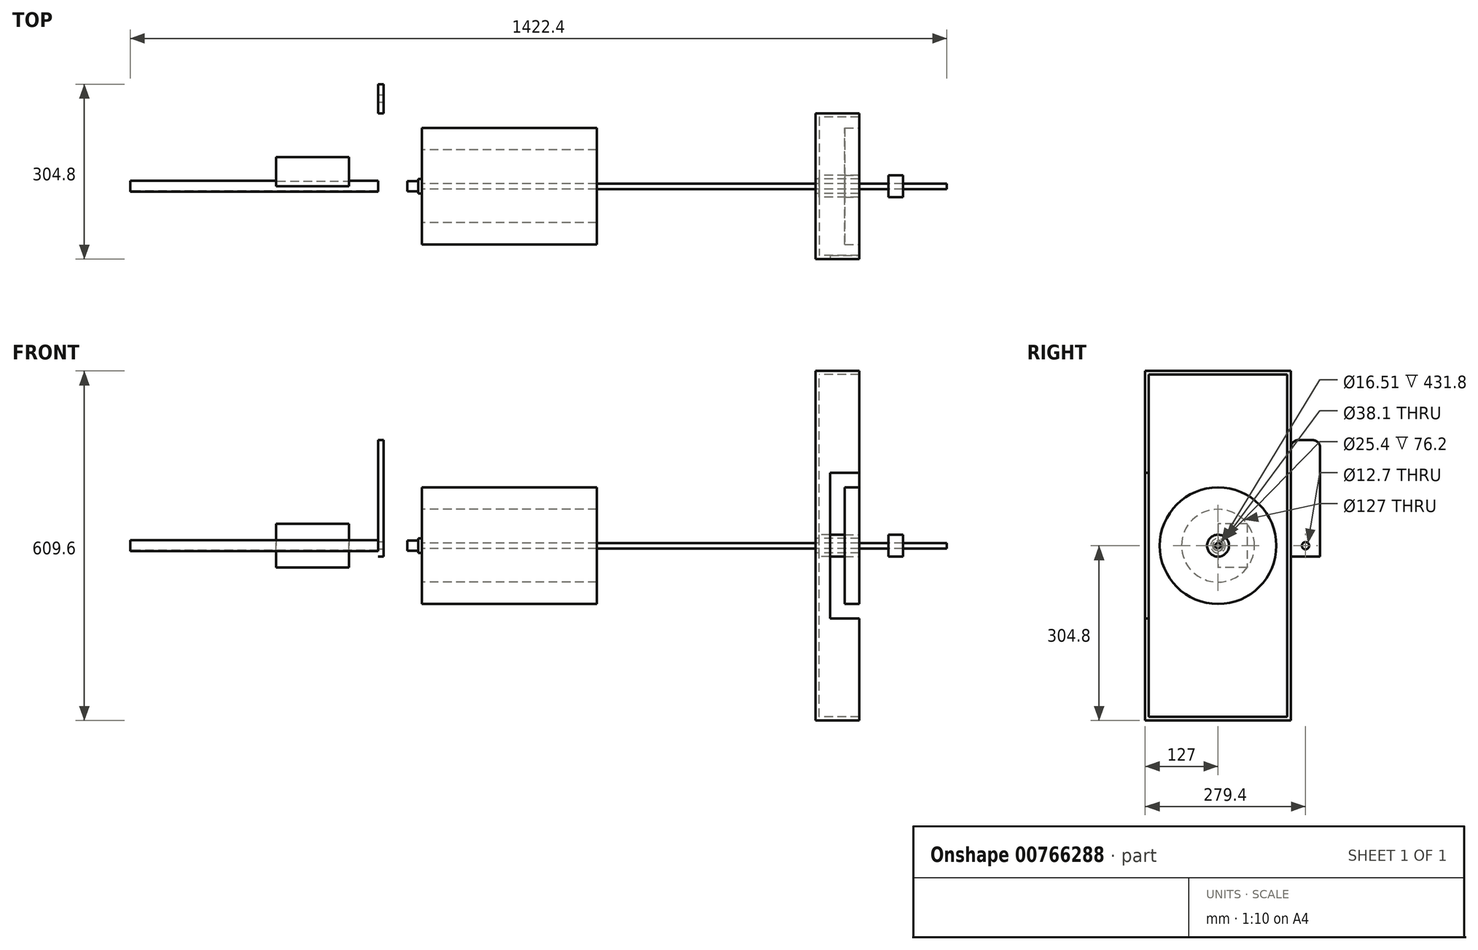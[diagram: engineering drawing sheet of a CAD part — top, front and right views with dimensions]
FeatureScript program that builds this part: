
annotation { "Feature Type Name" : "Feature", "Feature Type Description" : "" }
export const myFeature = defineFeature(function(context is Context, id is Id, definition is map)
    precondition{}
    {
        {
            var Q0;
            Q0=qCreatedBy(makeId("Right.planeOp"),FACE);
            var sketch = newSketch(context, id + "F0", { "sketchPlane" : qUnion([Q0])});
            skCircle(sketch, "E0", {"center": v(0, 0) * mm, "radius": 4.76 * mm});
            skSolve(sketch);
        }
        {
            var Q0;
            Q0=makeQuery(id+"F0.imprint","IMPRINT",FACE,{"disambiguationData":[TD([[makeQuery(id+"F0.imprint","IMPRINT",EDGE,{"derivedFrom":sQuery(id+"F0.wireOp",EDGE,"E0")}),1.0]])]});
            extrude(context, id + "F1", {"entities" : qUnion([Q0]), "depth" : 914.4 * mm, "offsetDistance" : 25.4 * mm});
        }
        {
            var Q0;
            Q0=qCreatedBy(makeId("Right.planeOp"),FACE);
            cPlane(context, id + "F2", {"entities" : qUnion([Q0]), "cplaneType" : CPlaneType.OFFSET, "offset" : 838.2 * mm, "width" : 152.4 * mm, "height" : 152.4 * mm});
        }
        {
            var Q0;
            Q0=qCreatedBy(id+"F2.planeOp",FACE);
            var sketch = newSketch(context, id + "F3", { "sketchPlane" : qUnion([Q0])});
            skCircle(sketch, "E1", {"center": v(0, 0) * mm, "radius": 19.05 * mm});
            skSolve(sketch);
        }
        {
            var Q0;
            Q0=makeQuery(id+"F3.imprint","IMPRINT",FACE,{"disambiguationData":[TD([[makeQuery(id+"F3.imprint","IMPRINT",EDGE,{"derivedFrom":sQuery(id+"F3.wireOp",EDGE,"E1")}),1.0]])]});
            extrude(context, id + "F4", {"entities" : qUnion([Q0]), "oppositeDirection" : true, "depth" : 25.4 * mm, "offsetDistance" : 25.4 * mm});
        }
        {
            var Q0;
            Q0=qCreatedBy(makeId("Right.planeOp"),FACE);
            var sketch = newSketch(context, id + "F5", { "sketchPlane" : qUnion([Q0])});
            skCircle(sketch, "E2", {"center": v(0, 0) * mm, "radius": 101.6 * mm});
            skCircle(sketch, "E3", {"center": v(0, 0) * mm, "radius": 63.5 * mm});
            skSolve(sketch);
        }
        {
            var Q0;
            Q0=makeQuery(id+"F5.imprint","IMPRINT",FACE,{"disambiguationData":[TD([[makeQuery(id+"F5.imprint","IMPRINT",EDGE,{"derivedFrom":sQuery(id+"F5.wireOp",EDGE,"E2")}),1.0]])]});
            extrude(context, id + "F6", {"entities" : qUnion([Q0]), "depth" : 304.8 * mm, "offsetDistance" : 25.4 * mm});
        }
        {
            var Q0;
            Q0=qCreatedBy(id+"F2.planeOp",FACE);
            cPlane(context, id + "F7", {"entities" : qUnion([Q0]), "cplaneType" : CPlaneType.OFFSET, "offset" : 152.4 * mm, "oppositeDirection" : true, "width" : 152.4 * mm, "height" : 152.4 * mm});
        }
        {
            var Q0;
            Q0=qCreatedBy(id+"F7.planeOp",FACE);
            var sketch = newSketch(context, id + "F8", { "sketchPlane" : qUnion([Q0])});
            skCircle(sketch, "E4", {"center": v(0, 0) * mm, "radius": 12.7 * mm});
            skLineSegment(sketch, "E5.bottom", {"start": v(127, -304.8) * mm, "end": v(-127, -304.8) * mm});
            skLineSegment(sketch, "E5.top", {"start": v(127, 304.8) * mm, "end": v(-127, 304.8) * mm});
            skLineSegment(sketch, "E5.left", {"start": v(127, -304.8) * mm, "end": v(127, 304.8) * mm});
            skLineSegment(sketch, "E5.right", {"start": v(-127, -304.8) * mm, "end": v(-127, 304.8) * mm});
            skSolve(sketch);
        }
        {
            var Q0;
            Q0=makeQuery(id+"F8.imprint","IMPRINT",FACE,{"disambiguationData":[TD([[makeQuery(id+"F8.imprint","IMPRINT",EDGE,{"derivedFrom":sQuery(id+"F8.wireOp",EDGE,"E4")}),-1.0]])]});
            extrude(context, id + "F9", {"entities" : qUnion([Q0]), "depth" : 76.2 * mm, "offsetDistance" : 25.4 * mm});
        }
        {
            var Q0;
            Q0=qCreatedBy(makeId("Right.planeOp"),FACE);
            cPlane(context, id + "F10", {"entities" : qUnion([Q0]), "cplaneType" : CPlaneType.OFFSET, "offset" : 254 * mm, "oppositeDirection" : true, "width" : 152.4 * mm, "height" : 152.4 * mm});
        }
        {
            var Q0;
            Q0=qCreatedBy(id+"F10.planeOp",FACE);
            var sketch = newSketch(context, id + "F11", { "sketchPlane" : qUnion([Q0])});
            skCircle(sketch, "E6", {"center": v(0, 0) * mm, "radius": 9.53 * mm});
            skLineSegment(sketch, "E7.bottom", {"start": v(50.8, 38.1) * mm, "end": v(-50.8, 38.1) * mm});
            skLineSegment(sketch, "E7.top", {"start": v(50.8, -38.1) * mm, "end": v(-50.8, -38.1) * mm});
            skLineSegment(sketch, "E7.left", {"start": v(50.8, 38.1) * mm, "end": v(50.8, -38.1) * mm});
            skLineSegment(sketch, "E7.right", {"start": v(-50.8, 38.1) * mm, "end": v(-50.8, -38.1) * mm});
            skLineSegment(sketch, "E8", {"start": v(0, 38.1) * mm, "end": v(0, -38.1) * mm});
            skSolve(sketch);
        }
        {
            var Q0;
            {var subQ0=sQuery(id+"F11.wireOp",EDGE,"E7.left");Q0=makeQuery(id+"F11.imprint","IMPRINT",FACE,{"disambiguationData":[TD([[makeQuery(id+"F11.imprint","IMPRINT",EDGE,{"derivedFrom":subQ0}),-1.0]])]});}
            extrude(context, id + "F12", {"entities" : qUnion([Q0]), "depth" : 127 * mm, "offsetDistance" : 25.4 * mm});
        }
        {
            var Q0;
            Q0=qCreatedBy(makeId("Right.planeOp"),FACE);
            cPlane(context, id + "F13", {"entities" : qUnion([Q0]), "cplaneType" : CPlaneType.OFFSET, "offset" : 76.2 * mm, "oppositeDirection" : true, "width" : 152.4 * mm, "height" : 152.4 * mm});
        }
        {
            var Q0;
            Q0=qCreatedBy(id+"F13.planeOp",FACE);
            var sketch = newSketch(context, id + "F14", { "sketchPlane" : qUnion([Q0])});
            skLineSegment(sketch, "E9.bottom", {"start": v(127, -19.05) * mm, "end": v(177.8, -19.05) * mm});
            skLineSegment(sketch, "E9.top", {"start": v(127, 184.15) * mm, "end": v(177.8, 184.15) * mm});
            skLineSegment(sketch, "E9.left", {"start": v(127, -19.05) * mm, "end": v(127, 184.15) * mm});
            skLineSegment(sketch, "E9.right", {"start": v(177.8, -19.05) * mm, "end": v(177.8, 184.15) * mm});
            skPoint(sketch, "E9.middle", {"position": v(152.4, 82.55) * mm});
            skCircle(sketch, "E10", {"center": v(152.4, 0) * mm, "radius": 6.35 * mm});
            skSolve(sketch);
        }
        {
            var Q0;
            Q0=makeQuery(id+"F14.imprint","IMPRINT",FACE,{"disambiguationData":[TD([[makeQuery(id+"F14.imprint","IMPRINT",EDGE,{"derivedFrom":sQuery(id+"F14.wireOp",EDGE,"E9.bottom")}),1.0]])]});
            extrude(context, id + "F15", {"entities" : qUnion([Q0]), "depth" : 9.52 * mm, "offsetDistance" : 25.4 * mm});
        }
        {
            var Q0;
            Q0=makeQuery(id+"F15.opExtrude","SWEPT_EDGE",EDGE,{"disambiguationData":[OSD([sQuery(id+"F14.wireOp",EDGE,"E9.top"),sQuery(id+"F14.wireOp",EDGE,"E9.right")])]});
            var Q1;
            Q1=makeQuery(id+"F15.opExtrude","SWEPT_EDGE",EDGE,{"disambiguationData":[OSD([sQuery(id+"F14.wireOp",EDGE,"E9.top"),sQuery(id+"F14.wireOp",EDGE,"E9.left")])]});
            fillet(context, id + "F16", {"entities" : qUnion([Q0, Q1]), "radius" : 12.7 * mm, "tangentPropagation" : true, "allowEdgeOverflow" : false});
        }
        {
            var Q0;
            Q0=makeQuery(id+"F9.opExtrude","CAP_FACE",FACE,{"disambiguationData":[OSD([sQuery(id+"F8.wireOp",EDGE,"E4"),sQuery(id+"F8.wireOp",EDGE,"E5.bottom"),sQuery(id+"F8.wireOp",EDGE,"E5.top"),sQuery(id+"F8.wireOp",EDGE,"E5.left"),sQuery(id+"F8.wireOp",EDGE,"E5.right")])],"isStart":false});
            shell(context, id + "F17", {"entities" : qUnion([Q0]), "thickness" : 6.35 * mm});
        }
        {
            var Q0;
            {var subQ0=sQuery(id+"F8.wireOp",EDGE,"E5.right");var subQ1=sQuery(id+"F8.wireOp",EDGE,"E5.left");var subQ2=sQuery(id+"F8.wireOp",EDGE,"E5.top");var subQ3=sQuery(id+"F8.wireOp",EDGE,"E5.bottom");var subQ4=sQuery(id+"F8.wireOp",EDGE,"E4");Q0=makeQuery(id+"F17.opShell","OFFSET_FACE",FACE,{"disambiguationData":[OSD([subQ4,subQ3,subQ2,subQ1,subQ0]),TDD([makeQuery(id+"F9.opExtrude","CAP_FACE",FACE,{"disambiguationData":[OSD([subQ4,subQ3,subQ2,subQ1,subQ0])],"isStart":false})])]});}
            var sketch = newSketch(context, id + "F18", { "sketchPlane" : qUnion([Q0])});
            skCircle(sketch, "E11", {"center": v(0, 0) * mm, "radius": 101.6 * mm});
            skSolve(sketch);
        }
        {
            var Q0;
            Q0=makeQuery(id+"F18.imprint","IMPRINT",FACE,{"disambiguationData":[TD([[makeQuery(id+"F18.imprint","IMPRINT",EDGE,{"derivedFrom":sQuery(id+"F18.wireOp",EDGE,"E11")}),1.0]])]});
            extrude(context, id + "F19", {"entities" : qUnion([Q0]), "oppositeDirection" : true, "depth" : 25.4 * mm, "offsetDistance" : 25.4 * mm});
        }
        {
            var Q0;
            Q0=makeQuery(id+"F6.opExtrude","CAP_FACE",FACE,{"disambiguationData":[OSD([sQuery(id+"F5.wireOp",EDGE,"E2"),sQuery(id+"F5.wireOp",EDGE,"E3")])],"isStart":true});
            var sketch = newSketch(context, id + "F20", { "sketchPlane" : qUnion([Q0])});
            skCircle(sketch, "E12", {"center": v(0, 0) * mm, "radius": 12.7 * mm});
            skSolve(sketch);
        }
        {
            var Q0;
            Q0=makeQuery(id+"F20.imprint","IMPRINT",FACE,{"disambiguationData":[TD([[makeQuery(id+"F20.imprint","IMPRINT",EDGE,{"derivedFrom":sQuery(id+"F20.wireOp",EDGE,"E12")}),1.0]])]});
            extrude(context, id + "F21", {"entities" : qUnion([Q0]), "operationType" : NewBodyOperationType.ADD, "depth" : 25.4 * mm, "offsetDistance" : 25.4 * mm});
        }
        {
            var Q0;
            Q0=makeQuery(id+"F21.opExtrude","CAP_FACE",FACE,{"disambiguationData":[OSD([sQuery(id+"F20.wireOp",EDGE,"E12")])],"isStart":false});
            var sketch = newSketch(context, id + "F22", { "sketchPlane" : qUnion([Q0])});
            skCircle(sketch, "E13", {"center": v(0, 0) * mm, "radius": 8.9 * mm});
            skCircle(sketch, "E14", {"center": v(0, 0) * mm, "radius": 12.7 * mm});
            skSolve(sketch);
        }
        {
            var Q0;
            Q0=makeQuery(id+"F22.imprint","IMPRINT",FACE,{"disambiguationData":[TD([[makeQuery(id+"F22.imprint","IMPRINT",EDGE,{"derivedFrom":sQuery(id+"F22.wireOp",EDGE,"E13")}),-1.0]])]});
            extrude(context, id + "F23", {"entities" : qUnion([Q0]), "operationType" : NewBodyOperationType.REMOVE, "oppositeDirection" : true, "depth" : 19.05 * mm, "offsetDistance" : 25.4 * mm});
        }
        {
            var Q0;
            Q0=qCreatedBy(id+"F10.planeOp",FACE);
            cPlane(context, id + "F24", {"entities" : qUnion([Q0]), "cplaneType" : CPlaneType.OFFSET, "offset" : 254 * mm, "oppositeDirection" : true, "width" : 152.4 * mm, "height" : 152.4 * mm});
        }
        {
            var Q0;
            Q0=qCreatedBy(id+"F24.planeOp",FACE);
            var sketch = newSketch(context, id + "F25", { "sketchPlane" : qUnion([Q0])});
            skCircle(sketch, "E15", {"center": v(0, 0) * mm, "radius": 9.53 * mm});
            skCircle(sketch, "E16", {"center": v(0, 0) * mm, "radius": 8.26 * mm});
            skSolve(sketch);
        }
        {
            var Q0;
            Q0=makeQuery(id+"F25.imprint","IMPRINT",FACE,{"disambiguationData":[TD([[makeQuery(id+"F25.imprint","IMPRINT",EDGE,{"derivedFrom":sQuery(id+"F25.wireOp",EDGE,"E15")}),1.0]])]});
            var Q1;
            Q1=makeQuery(id+"F15.opExtrude","CAP_FACE",FACE,{"disambiguationData":[OSD([sQuery(id+"F14.wireOp",EDGE,"E9.bottom"),sQuery(id+"F14.wireOp",EDGE,"E9.top"),sQuery(id+"F14.wireOp",EDGE,"E9.left"),sQuery(id+"F14.wireOp",EDGE,"E9.right"),sQuery(id+"F14.wireOp",EDGE,"E10")])],"isStart":true});
            extrude(context, id + "F26", {"entities" : qUnion([Q0]), "operationType" : NewBodyOperationType.ADD, "endBound" : BoundingType.UP_TO_SURFACE, "depth" : 25.4 * mm, "endBoundEntityFace" : qUnion([Q1]), "offsetDistance" : 25.4 * mm});
        }
        {
            var Q0;
            Q0=makeQuery(id+"F9.opExtrude","SWEPT_FACE",FACE,{"disambiguationData":[OSD([sQuery(id+"F8.wireOp",EDGE,"E5.right")])]});
            var sketch = newSketch(context, id + "F27", { "sketchPlane" : qUnion([Q0])});
            skLineSegment(sketch, "E17.bottom", {"start": v(762, -127) * mm, "end": v(711.2, -127) * mm});
            skLineSegment(sketch, "E17.top", {"start": v(762, 127) * mm, "end": v(711.2, 127) * mm});
            skLineSegment(sketch, "E17.left", {"start": v(762, -127) * mm, "end": v(762, 127) * mm});
            skLineSegment(sketch, "E17.right", {"start": v(711.2, -127) * mm, "end": v(711.2, 127) * mm});
            skPoint(sketch, "E17.middle", {"position": v(736.6, 0) * mm});
            skSolve(sketch);
        }
        {
            var Q0;
            Q0=makeQuery(id+"F27.imprint","IMPRINT",FACE,{"disambiguationData":[TD([[makeQuery(id+"F27.imprint","IMPRINT",EDGE,{"derivedFrom":sQuery(id+"F27.wireOp",EDGE,"E17.bottom")}),-1.0]])]});
            var Q1;
            Q1=makeQuery(id+"F17.opShell","OFFSET_FACE",FACE,{"disambiguationData":[OSD([sQuery(id+"F8.wireOp",EDGE,"E5.right")])]});
            extrude(context, id + "F28", {"entities" : qUnion([Q0]), "operationType" : NewBodyOperationType.REMOVE, "endBound" : BoundingType.UP_TO_SURFACE, "oppositeDirection" : true, "depth" : 12.7 * mm, "endBoundEntityFace" : qUnion([Q1]), "offsetDistance" : 25.4 * mm, "hasSecondDirection" : true, "secondDirectionOppositeDirection" : true, "secondDirectionDepth" : 0 * mm});
        }
    });
